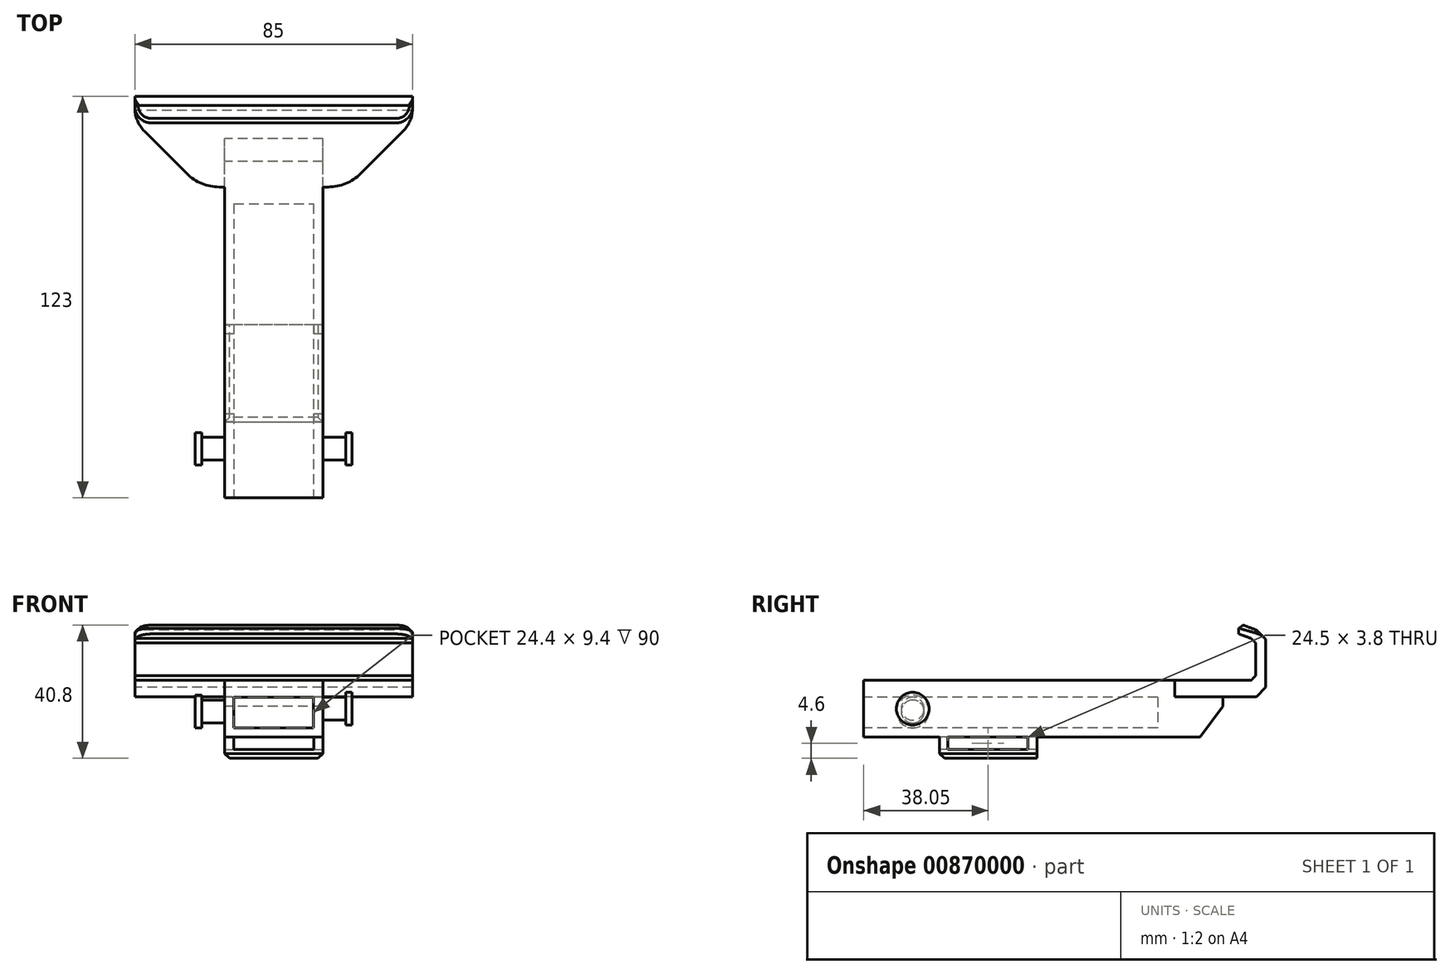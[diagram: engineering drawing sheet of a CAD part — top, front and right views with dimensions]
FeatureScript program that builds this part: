
annotation { "Feature Type Name" : "Feature", "Feature Type Description" : "" }
export const myFeature = defineFeature(function(context is Context, id is Id, definition is map)
    precondition{}
    {
        {
            var Q0;
            Q0=qCreatedBy(makeId("Right.planeOp"),FACE);
            var sketch = newSketch(context, id + "F0", { "sketchPlane" : qUnion([Q0])});
            skLineSegment(sketch, "E0.bottom", {"start": v(-30, 0) * mm, "end": v(60, 0) * mm});
            skLineSegment(sketch, "E0.top", {"start": v(-30, 17.4) * mm, "end": v(60, 17.4) * mm});
            skLineSegment(sketch, "E0.left", {"start": v(-30, 0) * mm, "end": v(-30, 17.4) * mm});
            skLineSegment(sketch, "E0.right", {"start": v(60, 0) * mm, "end": v(60, 17.4) * mm});
            skSolve(sketch);
        }
        {
            var Q0;
            Q0=makeQuery(id+"F0.imprint","IMPRINT",FACE,{"disambiguationData":[TD([[makeQuery(id+"F0.imprint","IMPRINT",EDGE,{"derivedFrom":sQuery(id+"F0.wireOp",EDGE,"E0.bottom")}),1.0]])]});
            extrude(context, id + "F1", {"entities" : qUnion([Q0]), "endBound" : BoundingType.SYMMETRIC, "depth" : 30 * mm, "offsetDistance" : 25 * mm});
        }
        {
            var Q0;
            Q0=makeQuery(id+"F1.opExtrude","SWEPT_FACE",FACE,{"disambiguationData":[OSD([sQuery(id+"F0.wireOp",EDGE,"E0.left")])]});
            var sketch = newSketch(context, id + "F2", { "sketchPlane" : qUnion([Q0])});
            skLineSegment(sketch, "E1.bottom", {"start": v(-12.2, 12.2) * mm, "end": v(12.2, 12.2) * mm});
            skLineSegment(sketch, "E1.top", {"start": v(-12.2, 2.8) * mm, "end": v(12.2, 2.8) * mm});
            skLineSegment(sketch, "E1.left", {"start": v(-12.2, 12.2) * mm, "end": v(-12.2, 2.8) * mm});
            skLineSegment(sketch, "E1.right", {"start": v(12.2, 12.2) * mm, "end": v(12.2, 2.8) * mm});
            skSolve(sketch);
        }
        {
            var Q0;
            Q0=makeQuery(id+"F2.imprint","IMPRINT",FACE,{"disambiguationData":[TD([[makeQuery(id+"F2.imprint","IMPRINT",EDGE,{"derivedFrom":sQuery(id+"F2.wireOp",EDGE,"E1.bottom")}),-1.0]])]});
            extrude(context, id + "F3", {"entities" : qUnion([Q0]), "operationType" : NewBodyOperationType.REMOVE, "oppositeDirection" : true, "depth" : 120 * mm, "offsetDistance" : 25 * mm});
        }
        {
            var Q0;
            Q0=qCreatedBy(makeId("Right.planeOp"),FACE);
            var sketch = newSketch(context, id + "F4", { "sketchPlane" : qUnion([Q0])});
            skLineSegment(sketch, "E2", {"start": v(60, 0) * mm, "end": v(73, 0) * mm});
            skLineSegment(sketch, "E3", {"start": v(73, 0) * mm, "end": v(80, 9.4) * mm});
            skLineSegment(sketch, "E4", {"start": v(80, 9.4) * mm, "end": v(80, 17.4) * mm});
            skLineSegment(sketch, "E5", {"start": v(80, 17.4) * mm, "end": v(60, 17.4) * mm});
            skLineSegment(sketch, "E6", {"start": v(60, 17.4) * mm, "end": v(60, 0) * mm});
            skSolve(sketch);
        }
        {
            var Q0;
            Q0=makeQuery(id+"F4.imprint","IMPRINT",FACE,{"disambiguationData":[TD([[makeQuery(id+"F4.imprint","IMPRINT",EDGE,{"derivedFrom":sQuery(id+"F4.wireOp",EDGE,"E2")}),1.0]])]});
            extrude(context, id + "F5", {"entities" : qUnion([Q0]), "operationType" : NewBodyOperationType.ADD, "endBound" : BoundingType.SYMMETRIC, "depth" : 30 * mm, "offsetDistance" : 25 * mm});
        }
        {
            var Q0;
            Q0=qCreatedBy(makeId("Right.planeOp"),FACE);
            var sketch = newSketch(context, id + "F6", { "sketchPlane" : qUnion([Q0])});
            skLineSegment(sketch, "E7", {"start": v(84.83, 31.6) * mm, "end": v(84.83, 34.79) * mm});
            skLineSegment(sketch, "E8", {"start": v(84.83, 34.79) * mm, "end": v(90.17, 32.84) * mm});
            skLineSegment(sketch, "E9", {"start": v(90.17, 32.84) * mm, "end": v(93, 30.02) * mm});
            skLineSegment(sketch, "E10", {"start": v(93, 30.02) * mm, "end": v(93, 15.23) * mm});
            skLineSegment(sketch, "E11", {"start": v(93, 15.23) * mm, "end": v(90.17, 12.4) * mm});
            skLineSegment(sketch, "E12", {"start": v(90.17, 12.4) * mm, "end": v(65.17, 12.4) * mm});
            skLineSegment(sketch, "E13", {"start": v(65.17, 12.4) * mm, "end": v(65.17, 17.4) * mm});
            skLineSegment(sketch, "E14", {"start": v(65.17, 17.4) * mm, "end": v(88.59, 17.4) * mm});
            skLineSegment(sketch, "E15", {"start": v(88.59, 17.4) * mm, "end": v(90, 18.81) * mm});
            skLineSegment(sketch, "E16", {"start": v(90, 18.81) * mm, "end": v(90, 28.81) * mm});
            skLineSegment(sketch, "E17", {"start": v(90, 28.81) * mm, "end": v(88.59, 30.23) * mm});
            skLineSegment(sketch, "E18", {"start": v(88.59, 30.23) * mm, "end": v(84.83, 31.6) * mm});
            skSolve(sketch);
        }
        {
            var Q0;
            Q0=makeQuery(id+"F6.imprint","IMPRINT",FACE,{"disambiguationData":[TD([[makeQuery(id+"F6.imprint","IMPRINT",EDGE,{"derivedFrom":sQuery(id+"F6.wireOp",EDGE,"E7")}),-1.0]])]});
            extrude(context, id + "F7", {"entities" : qUnion([Q0]), "operationType" : NewBodyOperationType.ADD, "endBound" : BoundingType.SYMMETRIC, "depth" : 85 * mm, "offsetDistance" : 25 * mm});
        }
        {
            var Q0;
            Q0=makeQuery(id+"F5.boolean.opBoolean","MERGE",FACE,{"derivedFrom":[makeQuery(id+"F1.opExtrude","CAP_FACE",FACE,{"disambiguationData":[OSD([sQuery(id+"F0.wireOp",EDGE,"E0.bottom"),sQuery(id+"F0.wireOp",EDGE,"E0.top"),sQuery(id+"F0.wireOp",EDGE,"E0.left"),sQuery(id+"F0.wireOp",EDGE,"E0.right")])],"isStart":false}),makeQuery(id+"F5.opExtrude","CAP_FACE",FACE,{"disambiguationData":[OSD([sQuery(id+"F4.wireOp",EDGE,"E2"),sQuery(id+"F4.wireOp",EDGE,"E3"),sQuery(id+"F4.wireOp",EDGE,"E4"),sQuery(id+"F4.wireOp",EDGE,"E5"),sQuery(id+"F4.wireOp",EDGE,"E6")])],"isStart":false})]});
            var sketch = newSketch(context, id + "F8", { "sketchPlane" : qUnion([Q0])});
            skCircle(sketch, "E19", {"center": v(-15, 8.7) * mm, "radius": 3.5 * mm});
            skSolve(sketch);
        }
        {
            var Q0;
            Q0=makeQuery(id+"F8.imprint","IMPRINT",FACE,{"disambiguationData":[TD([[makeQuery(id+"F8.imprint","IMPRINT",EDGE,{"derivedFrom":sQuery(id+"F8.wireOp",EDGE,"E19")}),1.0]])]});
            extrude(context, id + "F9", {"entities" : qUnion([Q0]), "operationType" : NewBodyOperationType.ADD, "depth" : 7 * mm, "offsetDistance" : 25 * mm});
        }
        {
            var Q0;
            Q0=makeQuery(id+"F9.opExtrude","CAP_FACE",FACE,{"disambiguationData":[OSD([sQuery(id+"F8.wireOp",EDGE,"E19")])],"isStart":false});
            var sketch = newSketch(context, id + "F10", { "sketchPlane" : qUnion([Q0])});
            skCircle(sketch, "E20", {"center": v(-15, 8.7) * mm, "radius": 5 * mm});
            skSolve(sketch);
        }
        {
            var Q0;
            Q0=makeQuery(id+"F10.imprint","IMPRINT",FACE,{"disambiguationData":[TD([[makeQuery(id+"F10.imprint","IMPRINT",EDGE,{"derivedFrom":sQuery(id+"F10.wireOp",EDGE,"E20")}),1.0]])]});
            var Q1;
            Q1=makeQuery(id+"F10.imprint","IMPRINT",FACE,{"disambiguationData":[TD([[makeQuery(id+"F10.imprint","IMPRINT",EDGE,{"derivedFrom":makeQuery(id+"F9.opExtrude","CAP_EDGE",EDGE,{"disambiguationData":[OSD([sQuery(id+"F8.wireOp",EDGE,"E19")])],"isStart":false})}),1.0]])]});
            extrude(context, id + "F11", {"entities" : qUnion([Q0, Q1]), "operationType" : NewBodyOperationType.ADD, "depth" : 2 * mm, "offsetDistance" : 25 * mm});
        }
        {
            var Q0;
            Q0=makeQuery(id+"F5.boolean.opBoolean","MERGE",FACE,{"derivedFrom":[makeQuery(id+"F1.opExtrude","CAP_FACE",FACE,{"disambiguationData":[OSD([sQuery(id+"F0.wireOp",EDGE,"E0.bottom"),sQuery(id+"F0.wireOp",EDGE,"E0.top"),sQuery(id+"F0.wireOp",EDGE,"E0.left"),sQuery(id+"F0.wireOp",EDGE,"E0.right")])],"isStart":true}),makeQuery(id+"F5.opExtrude","CAP_FACE",FACE,{"disambiguationData":[OSD([sQuery(id+"F4.wireOp",EDGE,"E2"),sQuery(id+"F4.wireOp",EDGE,"E3"),sQuery(id+"F4.wireOp",EDGE,"E4"),sQuery(id+"F4.wireOp",EDGE,"E5"),sQuery(id+"F4.wireOp",EDGE,"E6")])],"isStart":true})]});
            var sketch = newSketch(context, id + "F12", { "sketchPlane" : qUnion([Q0])});
            skCircle(sketch, "E21", {"center": v(15, 7.84) * mm, "radius": 3.5 * mm});
            skSolve(sketch);
        }
        {
            var Q0;
            Q0=makeQuery(id+"F12.imprint","IMPRINT",FACE,{"disambiguationData":[TD([[makeQuery(id+"F12.imprint","IMPRINT",EDGE,{"derivedFrom":sQuery(id+"F12.wireOp",EDGE,"E21")}),1.0]])]});
            extrude(context, id + "F13", {"entities" : qUnion([Q0]), "operationType" : NewBodyOperationType.ADD, "depth" : 7 * mm, "offsetDistance" : 25 * mm});
        }
        {
            var Q0;
            Q0=makeQuery(id+"F13.opExtrude","CAP_FACE",FACE,{"disambiguationData":[OSD([sQuery(id+"F12.wireOp",EDGE,"E21")])],"isStart":false});
            var sketch = newSketch(context, id + "F14", { "sketchPlane" : qUnion([Q0])});
            skCircle(sketch, "E22", {"center": v(15, 7.84) * mm, "radius": 5 * mm});
            skSolve(sketch);
        }
        {
            var Q0;
            Q0 = qSketchRegion(id + "F14", true);
            extrude(context, id + "F15", {"entities" : qUnion([Q0]), "operationType" : NewBodyOperationType.ADD, "depth" : 2 * mm, "offsetDistance" : 25 * mm});
        }
        {
            var Q0;
            Q0=qCreatedBy(makeId("Right.planeOp"),FACE);
            var sketch = newSketch(context, id + "F16", { "sketchPlane" : qUnion([Q0])});
            skLineSegment(sketch, "E23.bottom", {"start": v(-6.8, 0) * mm, "end": v(23, 0) * mm});
            skLineSegment(sketch, "E23.top", {"start": v(-6.8, -6.5) * mm, "end": v(23, -6.5) * mm});
            skLineSegment(sketch, "E23.left", {"start": v(-6.8, 0) * mm, "end": v(-6.8, -6.5) * mm});
            skLineSegment(sketch, "E23.right", {"start": v(23, 0) * mm, "end": v(23, -6.5) * mm});
            skSolve(sketch);
        }
        {
            var Q0;
            Q0=makeQuery(id+"F16.imprint","IMPRINT",FACE,{"disambiguationData":[TD([[makeQuery(id+"F16.imprint","IMPRINT",EDGE,{"derivedFrom":sQuery(id+"F16.wireOp",EDGE,"E23.bottom")}),-1.0]])]});
            extrude(context, id + "F17", {"entities" : qUnion([Q0]), "operationType" : NewBodyOperationType.ADD, "endBound" : BoundingType.SYMMETRIC, "depth" : 30 * mm, "offsetDistance" : 25 * mm});
        }
        {
            var Q0;
            Q0=makeQuery(id+"F17.boolean.opBoolean","MERGE",FACE,{"derivedFrom":[makeQuery(id+"F5.boolean.opBoolean","MERGE",FACE,{"derivedFrom":[makeQuery(id+"F1.opExtrude","CAP_FACE",FACE,{"disambiguationData":[OSD([sQuery(id+"F0.wireOp",EDGE,"E0.bottom"),sQuery(id+"F0.wireOp",EDGE,"E0.top"),sQuery(id+"F0.wireOp",EDGE,"E0.left"),sQuery(id+"F0.wireOp",EDGE,"E0.right")])],"isStart":false}),makeQuery(id+"F5.opExtrude","CAP_FACE",FACE,{"disambiguationData":[OSD([sQuery(id+"F4.wireOp",EDGE,"E2"),sQuery(id+"F4.wireOp",EDGE,"E3"),sQuery(id+"F4.wireOp",EDGE,"E4"),sQuery(id+"F4.wireOp",EDGE,"E5"),sQuery(id+"F4.wireOp",EDGE,"E6")])],"isStart":false})]}),makeQuery(id+"F17.opExtrude","CAP_FACE",FACE,{"disambiguationData":[OSD([sQuery(id+"F16.wireOp",EDGE,"E23.bottom"),sQuery(id+"F16.wireOp",EDGE,"E23.top"),sQuery(id+"F16.wireOp",EDGE,"E23.left"),sQuery(id+"F16.wireOp",EDGE,"E23.right")])],"isStart":false})]});
            var sketch = newSketch(context, id + "F18", { "sketchPlane" : qUnion([Q0])});
            skLineSegment(sketch, "E24.bottom", {"start": v(-4.2, 0) * mm, "end": v(20.3, 0) * mm});
            skLineSegment(sketch, "E24.top", {"start": v(-4.2, -3.8) * mm, "end": v(20.3, -3.8) * mm});
            skLineSegment(sketch, "E24.left", {"start": v(-4.2, 0) * mm, "end": v(-4.2, -3.8) * mm});
            skLineSegment(sketch, "E24.right", {"start": v(20.3, 0) * mm, "end": v(20.3, -3.8) * mm});
            skSolve(sketch);
        }
        {
            var Q0;
            Q0 = qSketchRegion(id + "F18", true);
            extrude(context, id + "F19", {"entities" : qUnion([Q0]), "operationType" : NewBodyOperationType.REMOVE, "oppositeDirection" : true, "depth" : 31 * mm, "offsetDistance" : 25 * mm});
        }
        {
            var Q0;
            Q0=makeQuery(id+"F17.opExtrude","SWEPT_FACE",FACE,{"disambiguationData":[OSD([sQuery(id+"F16.wireOp",EDGE,"E23.left")])]});
            var sketch = newSketch(context, id + "F20", { "sketchPlane" : qUnion([Q0])});
            skLineSegment(sketch, "E25.bottom", {"start": v(-12.3, 0) * mm, "end": v(12.3, 0) * mm});
            skLineSegment(sketch, "E25.top", {"start": v(-12.3, -3.8) * mm, "end": v(12.3, -3.8) * mm});
            skLineSegment(sketch, "E25.left", {"start": v(-12.3, 0) * mm, "end": v(-12.3, -3.8) * mm});
            skLineSegment(sketch, "E25.right", {"start": v(12.3, 0) * mm, "end": v(12.3, -3.8) * mm});
            skSolve(sketch);
        }
        {
            var Q0;
            Q0 = qSketchRegion(id + "F20", true);
            extrude(context, id + "F21", {"entities" : qUnion([Q0]), "operationType" : NewBodyOperationType.REMOVE, "oppositeDirection" : true, "depth" : 31 * mm, "offsetDistance" : 25 * mm});
        }
        {
            var Q0;
            Q0=makeQuery(id+"F17.opExtrude","SWEPT_EDGE",EDGE,{"disambiguationData":[OSD([sQuery(id+"F16.wireOp",EDGE,"E23.top"),sQuery(id+"F16.wireOp",EDGE,"E23.left")])]});
            chamfer(context, id + "F22", {"entities" : qUnion([Q0]), "width" : 1.5 * mm, "tangentPropagation" : true});
        }
        {
            var Q0;
            Q0=makeQuery(id+"F17.opExtrude","CAP_EDGE",EDGE,{"disambiguationData":[OSD([sQuery(id+"F16.wireOp",EDGE,"E23.top")])],"isStart":false});
            var Q1;
            Q1=makeQuery(id+"F17.opExtrude","CAP_EDGE",EDGE,{"disambiguationData":[OSD([sQuery(id+"F16.wireOp",EDGE,"E23.top")])],"isStart":true});
            var Q2;
            Q2=makeQuery(id+"F3.boolean.opBoolean","COPY",EDGE,{"derivedFrom":makeQuery(id+"F3.opExtrude","CAP_EDGE",EDGE,{"disambiguationData":[OSD([sQuery(id+"F2.wireOp",EDGE,"E1.bottom")])],"isStart":true})});
            var Q3;
            Q3=makeQuery(id+"F3.boolean.opBoolean","COPY",EDGE,{"derivedFrom":makeQuery(id+"F3.opExtrude","CAP_EDGE",EDGE,{"disambiguationData":[OSD([sQuery(id+"F2.wireOp",EDGE,"E1.right")])],"isStart":true})});
            var Q4;
            Q4=makeQuery(id+"F3.boolean.opBoolean","COPY",EDGE,{"derivedFrom":makeQuery(id+"F3.opExtrude","CAP_EDGE",EDGE,{"disambiguationData":[OSD([sQuery(id+"F2.wireOp",EDGE,"E1.left")])],"isStart":true})});
            var Q5;
            Q5=makeQuery(id+"F3.boolean.opBoolean","COPY",EDGE,{"derivedFrom":makeQuery(id+"F3.opExtrude","CAP_EDGE",EDGE,{"disambiguationData":[OSD([sQuery(id+"F2.wireOp",EDGE,"E1.top")])],"isStart":true})});
            chamfer(context, id + "F23", {"entities" : qUnion([Q0, Q1, Q2, Q3, Q4, Q5]), "width" : 1.5 * mm, "tangentPropagation" : true});
        }
        {
            var Q0;
            Q0=makeQuery(id+"F7.opExtrude","CAP_EDGE",EDGE,{"disambiguationData":[OSD([sQuery(id+"F6.wireOp",EDGE,"E13")])],"isStart":true});
            var Q1;
            Q1=makeQuery(id+"F7.opExtrude","CAP_EDGE",EDGE,{"disambiguationData":[OSD([sQuery(id+"F6.wireOp",EDGE,"E13")])],"isStart":false});
            chamfer(context, id + "F24", {"entities" : qUnion([Q0, Q1]), "width" : 20 * mm, "tangentPropagation" : true});
        }
        {
            var Q0;
            {var subQ2=sQuery(id+"F0.wireOp",EDGE,"E0.top");var subQ4=sQuery(id+"F6.wireOp",EDGE,"E13");Q0=makeQuery(id+"F24.opChamfer","BLEND_EDGE",EDGE,{"blendedFrom":[makeQuery(id+"F7.opExtrude","CAP_EDGE",EDGE,{"disambiguationData":[OSD([subQ4])],"isStart":true}),makeQuery(id+"F7.boolean.opBoolean","SPLIT",FACE,{"disambiguationData":[TD([makeQuery(id+"F1.opExtrude","CAP_FACE",FACE,{"disambiguationData":[OSD([sQuery(id+"F0.wireOp",EDGE,"E0.bottom"),subQ2,sQuery(id+"F0.wireOp",EDGE,"E0.left"),sQuery(id+"F0.wireOp",EDGE,"E0.right")])],"isStart":true})])],"derivedFrom":makeQuery(id+"F7.opExtrude","SWEPT_FACE",FACE,{"disambiguationData":[OSD([subQ4])]})})],"blendedInto":[makeQuery(id+"F7.boolean.opBoolean","SPLIT",FACE,{"disambiguationData":[TD([makeQuery(id+"F1.opExtrude","CAP_FACE",FACE,{"disambiguationData":[OSD([sQuery(id+"F0.wireOp",EDGE,"E0.bottom"),subQ2,sQuery(id+"F0.wireOp",EDGE,"E0.left"),sQuery(id+"F0.wireOp",EDGE,"E0.right")])],"isStart":true})])],"derivedFrom":makeQuery(id+"F7.opExtrude","SWEPT_FACE",FACE,{"disambiguationData":[OSD([subQ4])]})})]});}
            var Q1;
            {var subQ1=sQuery(id+"F0.wireOp",EDGE,"E0.top");var subQ3=sQuery(id+"F6.wireOp",EDGE,"E13");Q1=makeQuery(id+"F24.opChamfer","BLEND_EDGE",EDGE,{"blendedFrom":[makeQuery(id+"F7.opExtrude","CAP_EDGE",EDGE,{"disambiguationData":[OSD([subQ3])],"isStart":false}),makeQuery(id+"F7.boolean.opBoolean","SPLIT",FACE,{"disambiguationData":[TD([makeQuery(id+"F1.opExtrude","CAP_FACE",FACE,{"disambiguationData":[OSD([sQuery(id+"F0.wireOp",EDGE,"E0.bottom"),subQ1,sQuery(id+"F0.wireOp",EDGE,"E0.left"),sQuery(id+"F0.wireOp",EDGE,"E0.right")])],"isStart":false})])],"derivedFrom":makeQuery(id+"F7.opExtrude","SWEPT_FACE",FACE,{"disambiguationData":[OSD([subQ3])]})})],"blendedInto":[makeQuery(id+"F7.boolean.opBoolean","SPLIT",FACE,{"disambiguationData":[TD([makeQuery(id+"F1.opExtrude","CAP_FACE",FACE,{"disambiguationData":[OSD([sQuery(id+"F0.wireOp",EDGE,"E0.bottom"),subQ1,sQuery(id+"F0.wireOp",EDGE,"E0.left"),sQuery(id+"F0.wireOp",EDGE,"E0.right")])],"isStart":false})])],"derivedFrom":makeQuery(id+"F7.opExtrude","SWEPT_FACE",FACE,{"disambiguationData":[OSD([subQ3])]})})]});}
            fillet(context, id + "F25", {"entities" : qUnion([Q0, Q1]), "radius" : 14 * mm, "tangentPropagation" : true, "allowEdgeOverflow" : false});
        }
        {
            var Q0;
            {var subQ0=sQuery(id+"F6.wireOp",EDGE,"E13");Q0=makeQuery(id+"F24.opChamfer","BLEND_EDGE",EDGE,{"blendedFrom":[makeQuery(id+"F7.opExtrude","CAP_EDGE",EDGE,{"disambiguationData":[OSD([subQ0])],"isStart":true}),makeQuery(id+"F7.opExtrude","CAP_FACE",FACE,{"disambiguationData":[OSD([sQuery(id+"F6.wireOp",EDGE,"E7"),sQuery(id+"F6.wireOp",EDGE,"E8"),sQuery(id+"F6.wireOp",EDGE,"E9"),sQuery(id+"F6.wireOp",EDGE,"E10"),sQuery(id+"F6.wireOp",EDGE,"E11"),sQuery(id+"F6.wireOp",EDGE,"E12"),subQ0,sQuery(id+"F6.wireOp",EDGE,"E14"),sQuery(id+"F6.wireOp",EDGE,"E15"),sQuery(id+"F6.wireOp",EDGE,"E16"),sQuery(id+"F6.wireOp",EDGE,"E17"),sQuery(id+"F6.wireOp",EDGE,"E18")])],"isStart":true})],"blendedInto":[makeQuery(id+"F7.opExtrude","CAP_FACE",FACE,{"disambiguationData":[OSD([sQuery(id+"F6.wireOp",EDGE,"E7"),sQuery(id+"F6.wireOp",EDGE,"E8"),sQuery(id+"F6.wireOp",EDGE,"E9"),sQuery(id+"F6.wireOp",EDGE,"E10"),sQuery(id+"F6.wireOp",EDGE,"E11"),sQuery(id+"F6.wireOp",EDGE,"E12"),subQ0,sQuery(id+"F6.wireOp",EDGE,"E14"),sQuery(id+"F6.wireOp",EDGE,"E15"),sQuery(id+"F6.wireOp",EDGE,"E16"),sQuery(id+"F6.wireOp",EDGE,"E17"),sQuery(id+"F6.wireOp",EDGE,"E18")])],"isStart":true})]});}
            var Q1;
            {var subQ0=sQuery(id+"F6.wireOp",EDGE,"E13");Q1=makeQuery(id+"F24.opChamfer","BLEND_EDGE",EDGE,{"blendedFrom":[makeQuery(id+"F7.opExtrude","CAP_EDGE",EDGE,{"disambiguationData":[OSD([subQ0])],"isStart":false}),makeQuery(id+"F7.opExtrude","CAP_FACE",FACE,{"disambiguationData":[OSD([sQuery(id+"F6.wireOp",EDGE,"E7"),sQuery(id+"F6.wireOp",EDGE,"E8"),sQuery(id+"F6.wireOp",EDGE,"E9"),sQuery(id+"F6.wireOp",EDGE,"E10"),sQuery(id+"F6.wireOp",EDGE,"E11"),sQuery(id+"F6.wireOp",EDGE,"E12"),subQ0,sQuery(id+"F6.wireOp",EDGE,"E14"),sQuery(id+"F6.wireOp",EDGE,"E15"),sQuery(id+"F6.wireOp",EDGE,"E16"),sQuery(id+"F6.wireOp",EDGE,"E17"),sQuery(id+"F6.wireOp",EDGE,"E18")])],"isStart":false})],"blendedInto":[makeQuery(id+"F7.opExtrude","CAP_FACE",FACE,{"disambiguationData":[OSD([sQuery(id+"F6.wireOp",EDGE,"E7"),sQuery(id+"F6.wireOp",EDGE,"E8"),sQuery(id+"F6.wireOp",EDGE,"E9"),sQuery(id+"F6.wireOp",EDGE,"E10"),sQuery(id+"F6.wireOp",EDGE,"E11"),sQuery(id+"F6.wireOp",EDGE,"E12"),subQ0,sQuery(id+"F6.wireOp",EDGE,"E14"),sQuery(id+"F6.wireOp",EDGE,"E15"),sQuery(id+"F6.wireOp",EDGE,"E16"),sQuery(id+"F6.wireOp",EDGE,"E17"),sQuery(id+"F6.wireOp",EDGE,"E18")])],"isStart":false})]});}
            fillet(context, id + "F26", {"entities" : qUnion([Q0, Q1]), "radius" : 10 * mm, "tangentPropagation" : true, "allowEdgeOverflow" : false});
        }
        {
            var Q0;
            Q0=makeQuery(id+"F7.opExtrude","CAP_EDGE",EDGE,{"disambiguationData":[OSD([sQuery(id+"F6.wireOp",EDGE,"E7")])],"isStart":false});
            var Q1;
            Q1=makeQuery(id+"F7.opExtrude","CAP_EDGE",EDGE,{"disambiguationData":[OSD([sQuery(id+"F6.wireOp",EDGE,"E7")])],"isStart":true});
            fillet(context, id + "F27", {"entities" : qUnion([Q0, Q1]), "radius" : 5 * mm, "tangentPropagation" : true, "allowEdgeOverflow" : false});
        }
        {
            var Q0;
            Q0=makeQuery(id+"F7.opExtrude","SWEPT_EDGE",EDGE,{"disambiguationData":[OSD([sQuery(id+"F6.wireOp",EDGE,"E7"),sQuery(id+"F6.wireOp",EDGE,"E8")])]});
            var Q1;
            Q1=makeQuery(id+"F27.opFillet","BLEND_EDGE",EDGE,{"blendedFrom":[makeQuery(id+"F7.opExtrude","CAP_EDGE",EDGE,{"disambiguationData":[OSD([sQuery(id+"F6.wireOp",EDGE,"E7")])],"isStart":false}),makeQuery(id+"F7.opExtrude","SWEPT_FACE",FACE,{"disambiguationData":[OSD([sQuery(id+"F6.wireOp",EDGE,"E8")])]})],"blendedInto":[makeQuery(id+"F7.opExtrude","SWEPT_FACE",FACE,{"disambiguationData":[OSD([sQuery(id+"F6.wireOp",EDGE,"E8")])]})]});
            var Q2;
            Q2=makeQuery(id+"F27.opFillet","BLEND_EDGE",EDGE,{"blendedFrom":[makeQuery(id+"F7.opExtrude","CAP_EDGE",EDGE,{"disambiguationData":[OSD([sQuery(id+"F6.wireOp",EDGE,"E7")])],"isStart":true}),makeQuery(id+"F7.opExtrude","SWEPT_FACE",FACE,{"disambiguationData":[OSD([sQuery(id+"F6.wireOp",EDGE,"E8")])]})],"blendedInto":[makeQuery(id+"F7.opExtrude","SWEPT_FACE",FACE,{"disambiguationData":[OSD([sQuery(id+"F6.wireOp",EDGE,"E8")])]})]});
            chamfer(context, id + "F28", {"entities" : qUnion([Q0, Q1, Q2]), "width" : 1 * mm, "tangentPropagation" : true});
        }
    });
